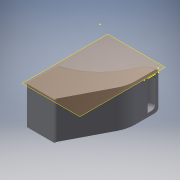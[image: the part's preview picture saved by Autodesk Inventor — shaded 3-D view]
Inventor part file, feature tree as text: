
AUTODESK INVENTOR PART (.ipt)
format: ipt  version: 2016 (Build 200138000, 138)  size: 857,088 bytes
history: native  units: mm
features: sketch x14, projected_geometry x13, extrude x11, fillet x10, reference x5, chamfer x2, plane x1, shell x1, imported_body x1, boolean_combine x1
ambient origin geometry x8: Origin, YZ Plane, XZ Plane, XY Plane, X Axis, Y Axis, Z Axis, Center Point
bodies: Solid1 (feature_tree), Solid2 (feature_tree)
feature tree (59):
  plane  "Work Plane1"
  extrude  "Extrusion1"  Depth=25.0mm TaperAngle=45.0deg
  chamfer  "Chamfer1"  Distance=2.0mm
  sketch  "Sketch2"  dims[d5=2.0mm]
  shell  "Shell1"  Thickness=3.0mm
  extrude  "Extrusion2"  Depth=2.0mm
  sketch  "Sketch4"  dims[d10=5.5mm d11=2.0mm d12=17.25mm d13=4.0mm d14=16.0mm d15=0.0mm d21=1.0mm d22=0.0mm]
  sketch  "Sketch5"  dims[d23=11.0mm d24=1.0mm d25=45.0deg d26=0.5mm d27=0.0mm]
  fillet  "Fillet1"  Radius=17.25mm
  fillet  "Fillet2"  Radius=4.0mm
  fillet  "Fillet3"  Radius=16.0mm
  fillet  "Fillet4"  Radius=1.0mm
  fillet  "Fillet5"  Radius=0.5mm
  extrude  "Extrusion3"  Depth=3.0mm TaperAngle=0.0deg
  extrude  "Extrusion5"  Depth=4.0mm TaperAngle=0.0deg
  chamfer  "Chamfer2"  Distance=3.0mm
  imported_body  "Base1"
  boolean_combine  "Combine1"
  extrude  "Extrusion6"  Depth=3.0mm TaperAngle=0.0deg
  extrude  "Extrusion7"  Depth=10.0mm
  extrude  "Extrusion8"  Depth=1.0mm
  extrude  "Extrusion9"  [1 undecoded]
  extrude  "Extrusion10"  [1 undecoded]
  extrude  "Extrusion11"  [1 undecoded]
  extrude  "Extrusion12"  [1 undecoded]
  fillet  "Fillet7"  [1 undecoded]
  fillet  "Fillet8"  [1 undecoded]
  fillet  "Fillet9"  [1 undecoded]
  fillet  "Fillet10"  [1 undecoded]
  fillet  "Fillet11"  [1 undecoded]
  sketch  "Sketch1"  dims[d0=20.0mm d1=0.0mm d2=25.0mm d3=13.0mm d4=45.0deg]
  sketch  "Sketch3"  dims[d6=8.0mm d7=2.0mm d8=0.0mm d9=3.0mm]
  reference  "Reference1"
  projected_geometry  "Projected Loop1"
  sketch  "Sketch6"  dims[d28=1.0mm d29=3.0mm d30=0.0mm]
  reference  "Reference2"
  reference  "Reference3"
  reference  "Reference4"
  reference  "Reference5"
  sketch  "Sketch8"  dims[d31=4.0mm d32=0.0mm d33=4.0mm d34=0.0mm d36=3.0mm d37=0.0mm]
  projected_geometry  "Projected Loop2"
  sketch  "Sketch9"  dims[d38=3.0mm d39=0.0mm d40=3.0mm d41=0.0mm]
  projected_geometry  "Projected Loop3"
  projected_geometry  "Projected Loop4"
  sketch  "Sketch10"  dims[d42=1.5mm d43=10.0mm]
  projected_geometry  "Projected Loop5"
  projected_geometry  "Projected Loop6"
  sketch  "Sketch11"  dims[d44=13.0mm d45=1.0mm]
  projected_geometry  "Projected Loop7"
  sketch  "Sketch12"  dims[d46=3.0mm]
  projected_geometry  "Projected Loop8"
  sketch  "Sketch13"
  projected_geometry  "Projected Loop9"
  sketch  "Sketch14"
  projected_geometry  "Projected Loop10"
  projected_geometry  "Projected Loop11"
  projected_geometry  "Projected Loop12"
  sketch  "Sketch15"
  projected_geometry  "Projected Loop13"
note: 9 required parameter values undecoded (feature->parameter linkage not recoverable at this tier; creation-order binding heuristic only, values carry confidence <= 0.55)
